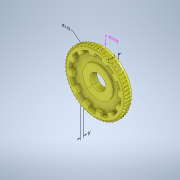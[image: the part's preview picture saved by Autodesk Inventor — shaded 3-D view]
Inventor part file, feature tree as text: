
AUTODESK INVENTOR PART (.ipt)
format: ipt  version: 2022.2 (Build 262287000, 287)  size: 1,359,360 bytes
history: native  units: mm (DEFAULTED — no unit token found)
features: other x25, sketch x7, extrude x6, plane x3, pattern_circular x2
ambient origin geometry x5: Origin, X Axis, Y Axis, Z Axis, Center Point
bodies: Solid1 (feature_tree)
feature tree (43):
  other  "Annotations"
  other  "Tooth Plane"
  other  "Base Body Sketch"
  other  "Base Body"
  other  "Base Body2"
  plane  "Work Plane13"
  other  "Tooth"
  pattern_circular  "Tooth Pattern"  Angle=90.0deg  [1 undecoded]
  plane  "Work Plane14"
  plane  "Work Plane15"
  extrude  "Extrusion2"  Depth=6.35mm
  extrude  "Extrusion3"  TaperAngle=360.0deg  [1 undecoded]
  extrude  "Extrusion7"  Depth=6.35mm
  pattern_circular  "Circular Pattern7"  [2 undecoded]
  extrude  "Extrusion8"  Depth=6.35mm TaperAngle=0.0deg
  extrude  "Extrusion9"  Depth=6.35mm
  extrude  "Extrusion10"  Depth=6.35mm
  other  "Tooth Sketch"
  sketch  "Sketch8"  dims[d35=90.0deg]
  other  "Srf1"
  sketch  "Sketch10"  dims[d37=-0.996687mm]
  sketch  "Sketch11"  dims[d38=56.595498mm]
  sketch  "Sketch16"  dims[d39=3.490659mm]
  other  "Work Axis2"
  other  "Work Axis3"
  other  "Work Axis4"
  other  "Work Axis5"
  other  "Work Axis6"
  other  "Work Axis7"
  other  "Work Axis8"
  other  "Work Axis9"
  other  "Work Axis10"
  other  "Work Axis11"
  other  "Work Axis12"
  sketch  "Sketch17"  dims[d40=6.144654mm]
  sketch  "Sketch18"  dims[d41=8.085071mm]
  sketch  "Sketch19"  dims[d42=1.524mm d43=90.0deg d44=600.0mm d46=360.0deg d50=5.130925mm d68=56.595498mm d69=0.0mm d73=0.0mm d75=0.523599mm d77=97.020853mm d78=9.525mm d79=0.0mm d80=0.0mm d81=0.0mm d82=0.0mm d83=0.523599mm d84=0.0mm d85=180.0deg d86=56.595498mm d87=101.871896mm d89=12.936114mm d90=90.0deg d92=9.525mm d93=56.595498mm d97=76.3905mm d98=0.0mm d99=0.0mm d102=25.781mm d103=94.869mm d104=6.35mm d105=0.0mm d151=0.087266mm d152=2.792527mm d153=5.177778mm d154=9.525mm d155=0.0mm d156=120.0mm d157=360.0deg d159=76.3905mm d160=86.746057mm d168=50.8mm d169=4.7625mm d170=0.0mm d171=88.9mm d172=5.08mm d173=5.08mm d174=2.54mm d175=0.0mm d180=3.175mm d181=0.0mm d161=16.054975mm d162=94.869mm d163=2.141741mm d164=8.066574mm d165=6.35mm d166=6.656436mm d167=25.781mm d177=7.715547mm d178=7.103274mm d179=9.525mm d182=2.118813mm d183=6.920726mm d184=6.35mm]
  other  "Pitch Diameter"
  other  "Diameter Dimension 1"
  other  "Linear Dimension 1"
  other  "Diameter Dimension 2"
  other  "Linear Dimension 2"
  other  "Linear Dimension 3"
note: 4 required parameter values undecoded (feature->parameter linkage not recoverable at this tier; creation-order binding heuristic only, values carry confidence <= 0.55)
